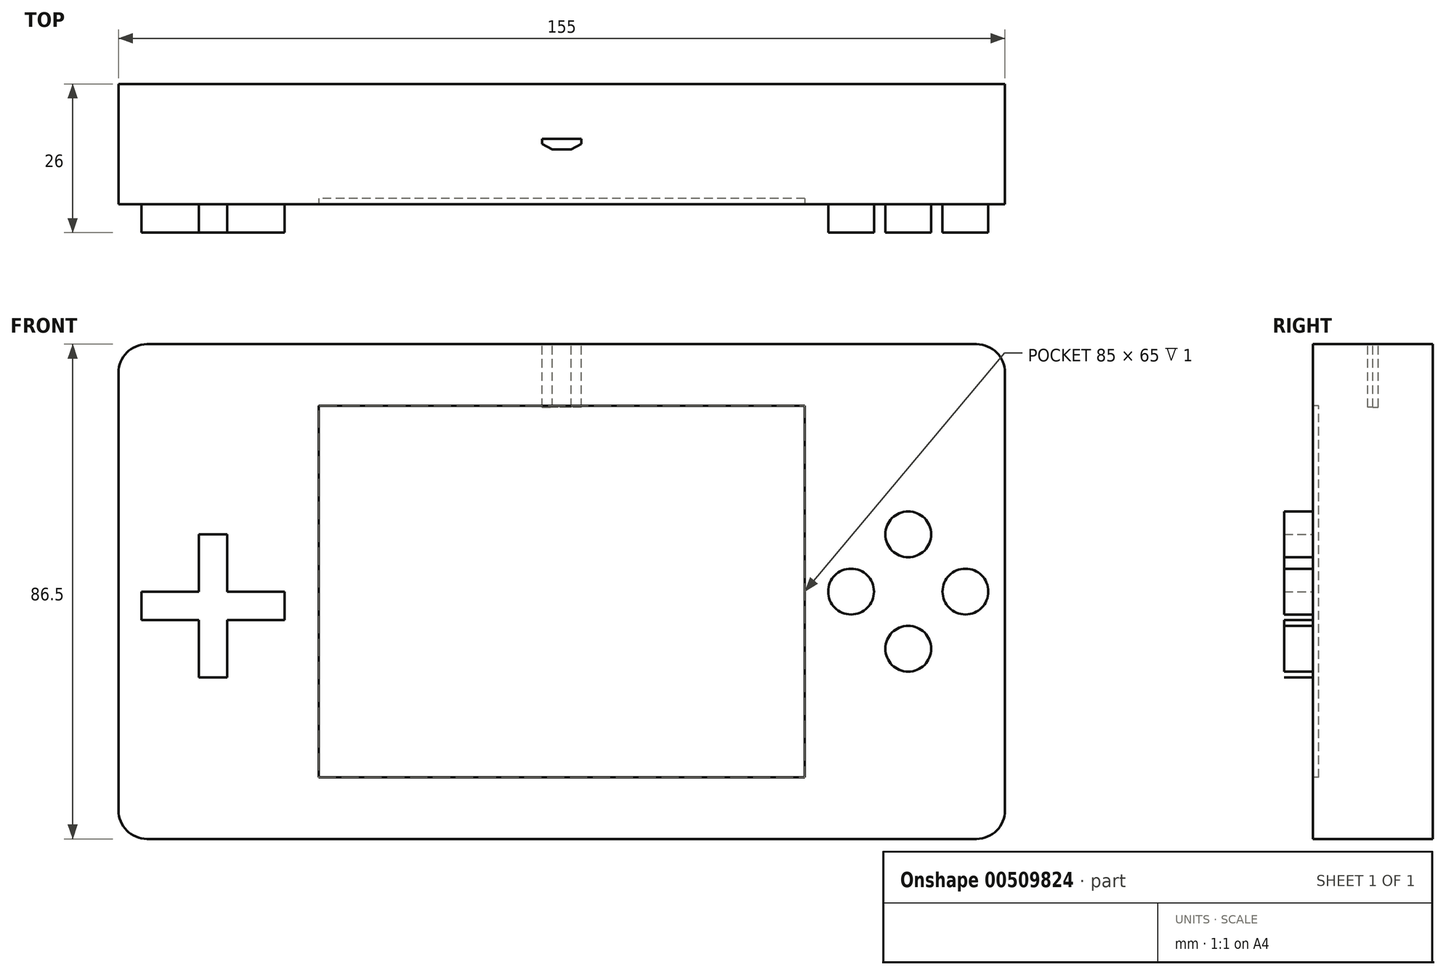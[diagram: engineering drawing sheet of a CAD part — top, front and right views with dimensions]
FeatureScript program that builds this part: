
annotation { "Feature Type Name" : "Feature", "Feature Type Description" : "" }
export const myFeature = defineFeature(function(context is Context, id is Id, definition is map)
    precondition{}
    {
        {
            var Q0;
            Q0=qCreatedBy(makeId("Front.planeOp"),FACE);
            var sketch = newSketch(context, id + "F0", { "sketchPlane" : qUnion([Q0])});
            skLineSegment(sketch, "E0.bottom", {"start": v(72.5, -43.25) * mm, "end": v(-72.5, -43.25) * mm});
            skLineSegment(sketch, "E0.top", {"start": v(72.5, 43.25) * mm, "end": v(-72.5, 43.25) * mm});
            skLineSegment(sketch, "E0.left", {"start": v(77.5, -38.25) * mm, "end": v(77.5, 38.25) * mm});
            skLineSegment(sketch, "E0.right", {"start": v(-77.5, -38.25) * mm, "end": v(-77.5, 38.25) * mm});
            skPoint(sketch, "E0.middle", {"position": v(0, 0) * mm});
            skPoint(sketch, "E1.visualSharp", {"position": v(77.5, 43.25) * mm});
            skArc(sketch, "E1.filletArc", {"start": v(77.5, 38.25) * mm, "mid": v(76.04, 41.79) * mm, "end": v(72.5, 43.25) * mm});
            skPoint(sketch, "E2.visualSharp", {"position": v(77.5, -43.25) * mm});
            skArc(sketch, "E2.filletArc", {"start": v(72.5, -43.25) * mm, "mid": v(76.04, -41.79) * mm, "end": v(77.5, -38.25) * mm});
            skPoint(sketch, "E3.visualSharp", {"position": v(-77.5, -43.25) * mm});
            skArc(sketch, "E3.filletArc", {"start": v(-77.5, -38.25) * mm, "mid": v(-76.04, -41.79) * mm, "end": v(-72.5, -43.25) * mm});
            skPoint(sketch, "E4.visualSharp", {"position": v(-77.5, 43.25) * mm});
            skArc(sketch, "E4.filletArc", {"start": v(-72.5, 43.25) * mm, "mid": v(-76.04, 41.79) * mm, "end": v(-77.5, 38.25) * mm});
            skSolve(sketch);
        }
        {
            var Q0;
            Q0=makeQuery(id+"F0.imprint","IMPRINT",FACE,{"disambiguationData":[TD([[makeQuery(id+"F0.imprint","IMPRINT",EDGE,{"derivedFrom":sQuery(id+"F0.wireOp",EDGE,"E0.bottom")}),-1.0]])]});
            extrude(context, id + "F1", {"entities" : qUnion([Q0]), "oppositeDirection" : true, "depth" : 21 * mm, "offsetDistance" : 25 * mm});
        }
        {
            var Q0;
            Q0=makeQuery(id+"F0.imprint","IMPRINT",FACE,{"disambiguationData":[TD([[makeQuery(id+"F0.imprint","IMPRINT",EDGE,{"derivedFrom":sQuery(id+"F0.wireOp",EDGE,"E0.bottom")}),-1.0]])]});
            var sketch = newSketch(context, id + "F2", { "sketchPlane" : qUnion([Q0])});
            skLineSegment(sketch, "E5.bottom", {"start": v(42.5, -32.5) * mm, "end": v(-42.5, -32.5) * mm});
            skLineSegment(sketch, "E5.top", {"start": v(42.5, 32.5) * mm, "end": v(-42.5, 32.5) * mm});
            skLineSegment(sketch, "E5.left", {"start": v(42.5, -32.5) * mm, "end": v(42.5, 32.5) * mm});
            skLineSegment(sketch, "E5.right", {"start": v(-42.5, -32.5) * mm, "end": v(-42.5, 32.5) * mm});
            skPoint(sketch, "E5.middle", {"position": v(0, 0) * mm});
            skSolve(sketch);
        }
        {
            var Q0;
            Q0=makeQuery(id+"F2.imprint","IMPRINT",FACE,{"disambiguationData":[TD([[makeQuery(id+"F2.imprint","IMPRINT",EDGE,{"derivedFrom":sQuery(id+"F2.wireOp",EDGE,"E5.bottom")}),1.0]])]});
            var sketch = newSketch(context, id + "F3", { "sketchPlane" : qUnion([Q0])});
            skLineSegment(sketch, "E6", {"start": v(-48.47, 0) * mm, "end": v(-58.47, 0) * mm});
            skLineSegment(sketch, "E7", {"start": v(-58.47, -15) * mm, "end": v(-58.47, -5) * mm});
            skLineSegment(sketch, "E8", {"start": v(-58.47, 0) * mm, "end": v(-48.47, 0) * mm});
            skLineSegment(sketch, "E9", {"start": v(-48.47, 0) * mm, "end": v(-48.47, -5) * mm});
            skLineSegment(sketch, "E10", {"start": v(-48.47, -5) * mm, "end": v(-58.47, -5) * mm});
            skLineSegment(sketch, "E11", {"start": v(-58.47, -5) * mm, "end": v(-58.47, -15) * mm});
            skLineSegment(sketch, "E12", {"start": v(-58.47, -15) * mm, "end": v(-63.47, -15) * mm});
            skLineSegment(sketch, "E13", {"start": v(-63.47, -15) * mm, "end": v(-63.47, -5) * mm});
            skLineSegment(sketch, "E14", {"start": v(-63.47, -5) * mm, "end": v(-73.47, -5) * mm});
            skLineSegment(sketch, "E15", {"start": v(-73.47, -5) * mm, "end": v(-73.47, 0) * mm});
            skLineSegment(sketch, "E16", {"start": v(-73.47, 0) * mm, "end": v(-63.47, 0) * mm});
            skLineSegment(sketch, "E17", {"start": v(-63.47, 0) * mm, "end": v(-63.47, 10) * mm});
            skLineSegment(sketch, "E18", {"start": v(-63.47, 10) * mm, "end": v(-58.47, 10) * mm});
            skLineSegment(sketch, "E19", {"start": v(-58.47, 10) * mm, "end": v(-58.47, 0) * mm});
            skPoint(sketch, "E20.orphan", {"position": v(-42.42, 0) * mm});
            skLineSegment(sketch, "E21.trimOffspring", {"start": v(-63.47, 0) * mm, "end": v(-73.47, 0) * mm});
            skLineSegment(sketch, "E22.trimOffspring", {"start": v(-58.47, 0) * mm, "end": v(-58.47, 10) * mm});
            skSolve(sketch);
        }
        {
            var Q0;
            Q0 = qSketchRegion(id + "F3", true);
            extrude(context, id + "F4", {"entities" : qUnion([Q0]), "operationType" : NewBodyOperationType.ADD, "depth" : 5 * mm, "offsetDistance" : 25 * mm});
        }
        {
            var Q0;
            Q0=qCreatedBy(makeId("Front.planeOp"),FACE);
            var sketch = newSketch(context, id + "F5", { "sketchPlane" : qUnion([Q0])});
            skLineSegment(sketch, "E23", {"start": v(50.58, 0) * mm, "end": v(54.58, 0) * mm});
            skLineSegment(sketch, "E24", {"start": v(54.58, 0) * mm, "end": v(50.58, 0) * mm});
            skPoint(sketch, "E25.orphan", {"position": v(43.08, 0) * mm});
            skPoint(sketch, "E26.orphan", {"position": v(78.08, 0) * mm});
            skCircle(sketch, "E27", {"center": v(60.58, 10) * mm, "radius": 4 * mm});
            skPoint(sketch, "E27.perimeterSnap0", {"position": v(65.58, 0) * mm});
            skPoint(sketch, "E27.perimeterSnap1", {"position": v(60.58, 5) * mm});
            skCircle(sketch, "E28", {"center": v(70.58, 0) * mm, "radius": 4 * mm});
            skCircle(sketch, "E29", {"center": v(60.58, -10) * mm, "radius": 4 * mm});
            skCircle(sketch, "E30", {"center": v(50.58, 0) * mm, "radius": 4 * mm});
            skPoint(sketch, "E31.orphan", {"position": v(60.58, 0) * mm});
            skSolve(sketch);
        }
        {
            var Q0;
            Q0 = qSketchRegion(id + "F5", true);
            extrude(context, id + "F6", {"entities" : qUnion([Q0]), "operationType" : NewBodyOperationType.ADD, "depth" : 5 * mm, "offsetDistance" : 25 * mm});
        }
        {
            var Q0;
            Q0=makeQuery(id+"F2.imprint","IMPRINT",FACE,{"disambiguationData":[TD([[makeQuery(id+"F2.imprint","IMPRINT",EDGE,{"derivedFrom":sQuery(id+"F2.wireOp",EDGE,"E5.bottom")}),-1.0]])]});
            extrude(context, id + "F7", {"entities" : qUnion([Q0]), "operationType" : NewBodyOperationType.REMOVE, "oppositeDirection" : true, "depth" : 1 * mm, "offsetDistance" : 25 * mm});
        }
        {
            var Q0;
            Q0=makeQuery(id+"F1.opExtrude","SWEPT_FACE",FACE,{"disambiguationData":[OSD([sQuery(id+"F0.wireOp",EDGE,"E0.top")])]});
            var sketch = newSketch(context, id + "F8", { "sketchPlane" : qUnion([Q0])});
            skLineSegment(sketch, "E32.bottom", {"start": v(1.68, 9.57) * mm, "end": v(-1.68, 9.57) * mm});
            skLineSegment(sketch, "E32.top", {"start": v(3.45, 11.42) * mm, "end": v(-3.45, 11.42) * mm});
            skLineSegment(sketch, "E32.left", {"start": v(3.45, 10.5) * mm, "end": v(3.45, 11.42) * mm});
            skLineSegment(sketch, "E32.right", {"start": v(-3.45, 10.5) * mm, "end": v(-3.45, 11.42) * mm});
            skPoint(sketch, "E32.middle", {"position": v(0, 10.5) * mm});
            skLineSegment(sketch, "E33", {"start": v(3.45, 10.5) * mm, "end": v(1.68, 9.57) * mm});
            skLineSegment(sketch, "E34", {"start": v(-3.45, 10.5) * mm, "end": v(-1.68, 9.57) * mm});
            skPoint(sketch, "E35.orphan", {"position": v(-3.45, 9.57) * mm});
            skPoint(sketch, "E36.orphan", {"position": v(3.45, 9.57) * mm});
            skPoint(sketch, "E37.trimOffspring.end.orphan", {"position": v(72.5, 10.5) * mm});
            skPoint(sketch, "E38.start.orphan", {"position": v(-72.5, 10.5) * mm});
            skSolve(sketch);
        }
        {
            var Q0;
            Q0 = qSketchRegion(id + "F8", true);
            extrude(context, id + "F9", {"entities" : qUnion([Q0]), "operationType" : NewBodyOperationType.REMOVE, "oppositeDirection" : true, "depth" : 11 * mm, "offsetDistance" : 25 * mm});
        }
    });
